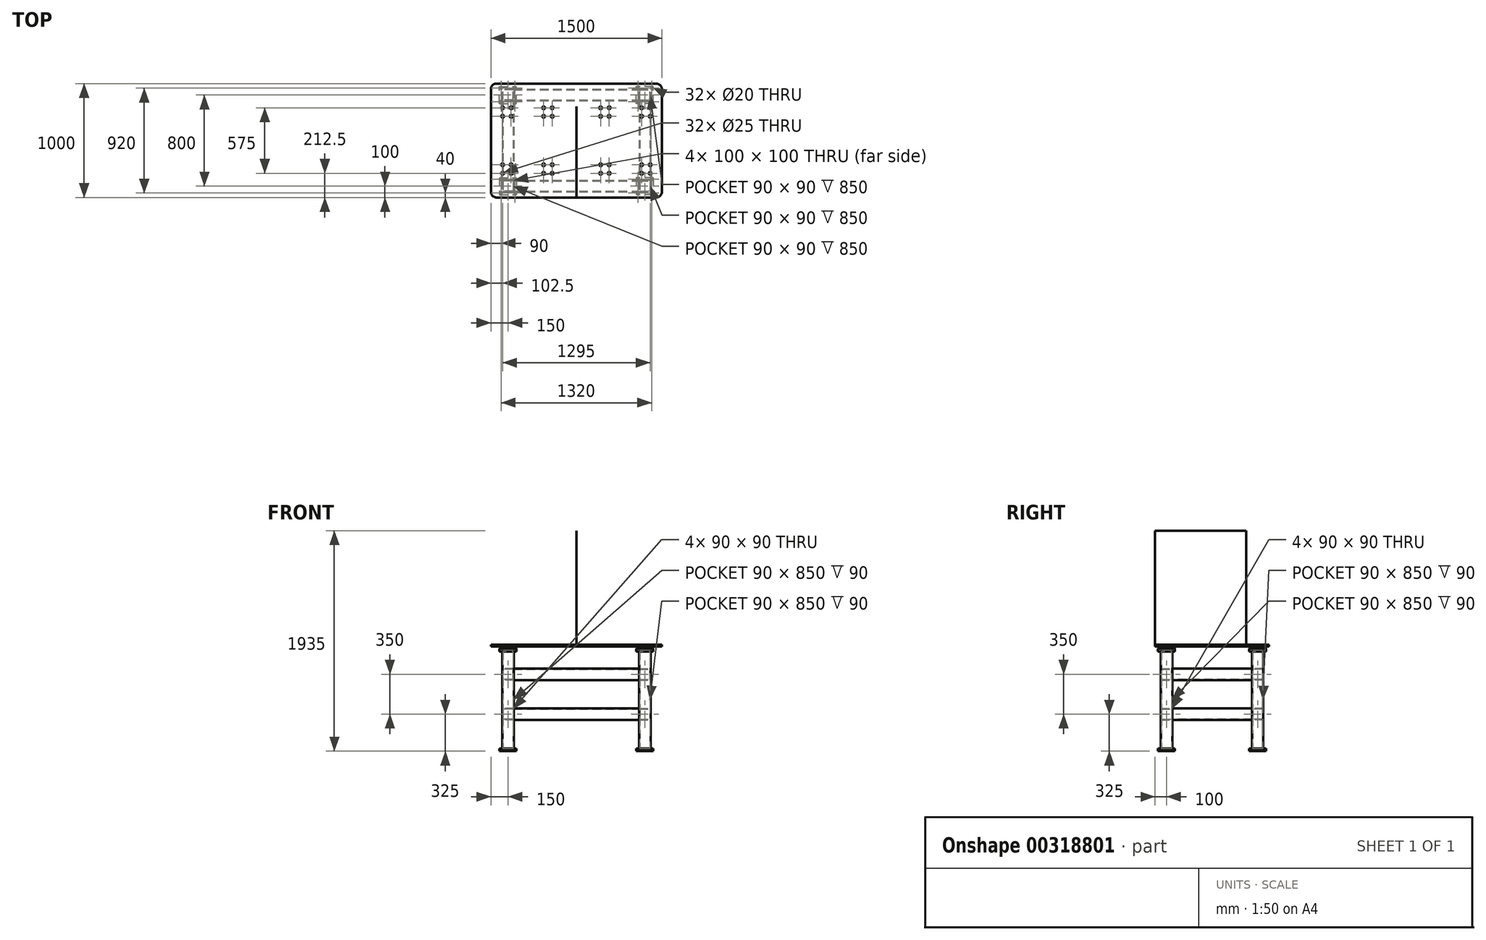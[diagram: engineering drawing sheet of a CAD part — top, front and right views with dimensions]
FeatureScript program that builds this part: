
annotation { "Feature Type Name" : "Feature", "Feature Type Description" : "" }
export const myFeature = defineFeature(function(context is Context, id is Id, definition is map)
    precondition{}
    {
        {
            var Q0;
            Q0=qCreatedBy(makeId("Top.planeOp"),FACE);
            var sketch = newSketch(context, id + "F0", { "sketchPlane" : qUnion([Q0])});
            skLineSegment(sketch, "E0.rect.bottom", {"start": v(-600, -400) * mm, "end": v(600, -400) * mm, "construction": true});
            skLineSegment(sketch, "E0.rect.top", {"start": v(-600, 400) * mm, "end": v(600, 400) * mm, "construction": true});
            skLineSegment(sketch, "E0.rect.left", {"start": v(-600, -400) * mm, "end": v(-600, 400) * mm, "construction": true});
            skLineSegment(sketch, "E0.rect.right", {"start": v(600, -400) * mm, "end": v(600, 400) * mm, "construction": true});
            skPoint(sketch, "E0.rect.middle", {"position": v(0, 0) * mm});
            skLineSegment(sketch, "E1.rect.bottom", {"start": v(-675, 325) * mm, "end": v(-525, 325) * mm});
            skLineSegment(sketch, "E1.rect.top", {"start": v(-675, 475) * mm, "end": v(-525, 475) * mm});
            skLineSegment(sketch, "E1.rect.left", {"start": v(-675, 325) * mm, "end": v(-675, 475) * mm});
            skLineSegment(sketch, "E1.rect.right", {"start": v(-525, 325) * mm, "end": v(-525, 475) * mm});
            skPoint(sketch, "E1.rect.middle", {"position": v(-600, 400) * mm});
            skLineSegment(sketch, "E2.rect.bottom", {"start": v(-660, 340) * mm, "end": v(-540, 340) * mm, "construction": true});
            skLineSegment(sketch, "E2.rect.top", {"start": v(-660, 460) * mm, "end": v(-540, 460) * mm, "construction": true});
            skLineSegment(sketch, "E2.rect.left", {"start": v(-660, 340) * mm, "end": v(-660, 460) * mm, "construction": true});
            skLineSegment(sketch, "E2.rect.right", {"start": v(-540, 340) * mm, "end": v(-540, 460) * mm, "construction": true});
            skCircle(sketch, "E3", {"center": v(-660, 460) * mm, "radius": 10 * mm});
            skCircle(sketch, "E4", {"center": v(-540, 460) * mm, "radius": 10 * mm});
            skCircle(sketch, "E5", {"center": v(-660, 340) * mm, "radius": 10 * mm});
            skCircle(sketch, "E6", {"center": v(-540, 340) * mm, "radius": 10 * mm});
            skCircle(sketch, "E7.MirrorC", {"center": v(540, 340) * mm, "radius": 10 * mm});
            skCircle(sketch, "E8.MirrorC", {"center": v(660, 460) * mm, "radius": 10 * mm});
            skCircle(sketch, "E9.MirrorC", {"center": v(660, 340) * mm, "radius": 10 * mm});
            skCircle(sketch, "E10.MirrorC", {"center": v(540, 460) * mm, "radius": 10 * mm});
            skPoint(sketch, "E11.MirrorP", {"position": v(600, 400) * mm});
            skLineSegment(sketch, "E12.MirrorCS", {"start": v(540, 340) * mm, "end": v(540, 460) * mm, "construction": true});
            skLineSegment(sketch, "E13.MirrorCS", {"start": v(660, 340) * mm, "end": v(660, 460) * mm, "construction": true});
            skLineSegment(sketch, "E14.MirrorCS", {"start": v(660, 460) * mm, "end": v(540, 460) * mm, "construction": true});
            skLineSegment(sketch, "E15.MirrorCS", {"start": v(675, 325) * mm, "end": v(525, 325) * mm});
            skLineSegment(sketch, "E16.MirrorCS", {"start": v(675, 475) * mm, "end": v(525, 475) * mm});
            skLineSegment(sketch, "E17.MirrorCS", {"start": v(675, 325) * mm, "end": v(675, 475) * mm});
            skLineSegment(sketch, "E18.MirrorCS", {"start": v(525, 325) * mm, "end": v(525, 475) * mm});
            skLineSegment(sketch, "E19.MirrorCS", {"start": v(660, 340) * mm, "end": v(540, 340) * mm, "construction": true});
            skCircle(sketch, "E20.MirrorC", {"center": v(540, -340) * mm, "radius": 10 * mm});
            skCircle(sketch, "E21.MirrorC", {"center": v(660, -340) * mm, "radius": 10 * mm});
            skCircle(sketch, "E22.MirrorC", {"center": v(-660, -460) * mm, "radius": 10 * mm});
            skCircle(sketch, "E23.MirrorC", {"center": v(-540, -340) * mm, "radius": 10 * mm});
            skCircle(sketch, "E24.MirrorC", {"center": v(-660, -340) * mm, "radius": 10 * mm});
            skCircle(sketch, "E25.MirrorC", {"center": v(-540, -460) * mm, "radius": 10 * mm});
            skCircle(sketch, "E26.MirrorC", {"center": v(660, -460) * mm, "radius": 10 * mm});
            skCircle(sketch, "E27.MirrorC", {"center": v(540, -460) * mm, "radius": 10 * mm});
            skPoint(sketch, "E28.MirrorP", {"position": v(600, -400) * mm});
            skPoint(sketch, "E29.MirrorP", {"position": v(-600, -400) * mm});
            skLineSegment(sketch, "E30.MirrorCS", {"start": v(540, -340) * mm, "end": v(540, -460) * mm, "construction": true});
            skLineSegment(sketch, "E31.MirrorCS", {"start": v(660, -460) * mm, "end": v(540, -460) * mm, "construction": true});
            skLineSegment(sketch, "E32.MirrorCS", {"start": v(675, -325) * mm, "end": v(525, -325) * mm});
            skLineSegment(sketch, "E33.MirrorCS", {"start": v(675, -325) * mm, "end": v(675, -475) * mm});
            skLineSegment(sketch, "E34.MirrorCS", {"start": v(660, -340) * mm, "end": v(540, -340) * mm, "construction": true});
            skLineSegment(sketch, "E35.MirrorCS", {"start": v(-540, -340) * mm, "end": v(-540, -460) * mm, "construction": true});
            skLineSegment(sketch, "E36.MirrorCS", {"start": v(-660, -340) * mm, "end": v(-660, -460) * mm, "construction": true});
            skLineSegment(sketch, "E37.MirrorCS", {"start": v(-660, -460) * mm, "end": v(-540, -460) * mm, "construction": true});
            skLineSegment(sketch, "E38.MirrorCS", {"start": v(-660, -340) * mm, "end": v(-540, -340) * mm, "construction": true});
            skLineSegment(sketch, "E39.MirrorCS", {"start": v(-525, -325) * mm, "end": v(-525, -475) * mm});
            skLineSegment(sketch, "E40.MirrorCS", {"start": v(-675, -325) * mm, "end": v(-675, -475) * mm});
            skLineSegment(sketch, "E41.MirrorCS", {"start": v(-675, -475) * mm, "end": v(-525, -475) * mm});
            skLineSegment(sketch, "E42.MirrorCS", {"start": v(-600, -400) * mm, "end": v(600, -400) * mm});
            skLineSegment(sketch, "E43.MirrorCS", {"start": v(525, -325) * mm, "end": v(525, -475) * mm});
            skLineSegment(sketch, "E44.MirrorCS", {"start": v(-675, -325) * mm, "end": v(-525, -325) * mm});
            skLineSegment(sketch, "E45.MirrorCS", {"start": v(660, -340) * mm, "end": v(660, -460) * mm, "construction": true});
            skLineSegment(sketch, "E46.MirrorCS", {"start": v(675, -475) * mm, "end": v(525, -475) * mm});
            skSolve(sketch);
        }
        {
            var Q0;
            Q0=qSketchRegion(id+"F0",true);
            extrude(context, id + "F1", {"entities" : qUnion([Q0]), "depth" : 25 * mm});
        }
        {
            var Q0;
            Q0=makeQuery(id+"F1.opExtrude","CAP_FACE",FACE,{"disambiguationData":[OSD([sQuery(id+"F0.wireOp",EDGE,"E1.rect.bottom"),sQuery(id+"F0.wireOp",EDGE,"E1.rect.top"),sQuery(id+"F0.wireOp",EDGE,"E1.rect.left"),sQuery(id+"F0.wireOp",EDGE,"E1.rect.right"),sQuery(id+"F0.wireOp",EDGE,"E3"),sQuery(id+"F0.wireOp",EDGE,"E4"),sQuery(id+"F0.wireOp",EDGE,"E5"),sQuery(id+"F0.wireOp",EDGE,"E6")])],"isStart":false});
            var sketch = newSketch(context, id + "F2", { "sketchPlane" : qUnion([Q0])});
            skLineSegment(sketch, "E47.rect.bottom", {"start": v(-550, 350) * mm, "end": v(-650, 350) * mm});
            skLineSegment(sketch, "E47.rect.top", {"start": v(-550, 450) * mm, "end": v(-650, 450) * mm});
            skLineSegment(sketch, "E47.rect.left", {"start": v(-550, 350) * mm, "end": v(-550, 450) * mm});
            skLineSegment(sketch, "E47.rect.right", {"start": v(-650, 350) * mm, "end": v(-650, 450) * mm});
            skPoint(sketch, "E47.rect.middle", {"position": v(-600, 400) * mm});
            skPoint(sketch, "E47.rect.middle.positionSnap0", {"position": v(-675, 400) * mm});
            skPoint(sketch, "E47.rect.centerSnap0", {"position": v(-675, 400) * mm});
            skLineSegment(sketch, "E48.rect.bottom", {"start": v(-555, 355) * mm, "end": v(-645, 355) * mm});
            skLineSegment(sketch, "E48.rect.top", {"start": v(-555, 445) * mm, "end": v(-645, 445) * mm});
            skLineSegment(sketch, "E48.rect.left", {"start": v(-555, 355) * mm, "end": v(-555, 445) * mm});
            skLineSegment(sketch, "E48.rect.right", {"start": v(-645, 355) * mm, "end": v(-645, 445) * mm});
            skPoint(sketch, "E49.MirrorP", {"position": v(600, 400) * mm});
            skPoint(sketch, "E50.MirrorP", {"position": v(675, 400) * mm});
            skLineSegment(sketch, "E51.MirrorCS", {"start": v(645, 355) * mm, "end": v(645, 445) * mm});
            skLineSegment(sketch, "E52.MirrorCS", {"start": v(555, 355) * mm, "end": v(555, 445) * mm});
            skLineSegment(sketch, "E53.MirrorCS", {"start": v(555, 445) * mm, "end": v(645, 445) * mm});
            skLineSegment(sketch, "E54.MirrorCS", {"start": v(555, 355) * mm, "end": v(645, 355) * mm});
            skLineSegment(sketch, "E55.MirrorCS", {"start": v(650, 350) * mm, "end": v(650, 450) * mm});
            skLineSegment(sketch, "E56.MirrorCS", {"start": v(550, 350) * mm, "end": v(650, 350) * mm});
            skLineSegment(sketch, "E57.MirrorCS", {"start": v(550, 350) * mm, "end": v(550, 450) * mm});
            skLineSegment(sketch, "E58.MirrorCS", {"start": v(550, 450) * mm, "end": v(650, 450) * mm});
            skLineSegment(sketch, "E59.MirrorCS", {"start": v(650, -350) * mm, "end": v(650, -450) * mm});
            skPoint(sketch, "E60.MirrorP", {"position": v(-675, -400) * mm});
            skPoint(sketch, "E61.MirrorP", {"position": v(600, -400) * mm});
            skPoint(sketch, "E62.MirrorP", {"position": v(-600, -400) * mm});
            skPoint(sketch, "E63.MirrorP", {"position": v(675, -400) * mm});
            skLineSegment(sketch, "E64.MirrorCS", {"start": v(-555, -355) * mm, "end": v(-555, -445) * mm});
            skLineSegment(sketch, "E65.MirrorCS", {"start": v(-555, -445) * mm, "end": v(-645, -445) * mm});
            skLineSegment(sketch, "E66.MirrorCS", {"start": v(-555, -355) * mm, "end": v(-645, -355) * mm});
            skLineSegment(sketch, "E67.MirrorCS", {"start": v(-650, -350) * mm, "end": v(-650, -450) * mm});
            skLineSegment(sketch, "E68.MirrorCS", {"start": v(-550, -350) * mm, "end": v(-550, -450) * mm});
            skLineSegment(sketch, "E69.MirrorCS", {"start": v(-550, -450) * mm, "end": v(-650, -450) * mm});
            skLineSegment(sketch, "E70.MirrorCS", {"start": v(-550, -350) * mm, "end": v(-650, -350) * mm});
            skLineSegment(sketch, "E71.MirrorCS", {"start": v(550, -450) * mm, "end": v(650, -450) * mm});
            skLineSegment(sketch, "E72.MirrorCS", {"start": v(550, -350) * mm, "end": v(550, -450) * mm});
            skLineSegment(sketch, "E73.MirrorCS", {"start": v(550, -350) * mm, "end": v(650, -350) * mm});
            skLineSegment(sketch, "E74.MirrorCS", {"start": v(-645, -355) * mm, "end": v(-645, -445) * mm});
            skLineSegment(sketch, "E75.MirrorCS", {"start": v(645, -355) * mm, "end": v(645, -445) * mm});
            skLineSegment(sketch, "E76.MirrorCS", {"start": v(555, -355) * mm, "end": v(555, -445) * mm});
            skLineSegment(sketch, "E77.MirrorCS", {"start": v(555, -355) * mm, "end": v(645, -355) * mm});
            skLineSegment(sketch, "E78.MirrorCS", {"start": v(555, -445) * mm, "end": v(645, -445) * mm});
            skSolve(sketch);
        }
        {
            var Q0;
            Q0=qSketchRegion(id+"F2",true);
            extrude(context, id + "F3", {"entities" : qUnion([Q0]), "operationType" : NewBodyOperationType.ADD, "depth" : 850 * mm});
        }
        {
            var Q0;
            Q0=makeQuery(id+"F3.opExtrude","CAP_FACE",FACE,{"disambiguationData":[OSD([sQuery(id+"F2.wireOp",EDGE,"E47.rect.bottom"),sQuery(id+"F2.wireOp",EDGE,"E47.rect.top"),sQuery(id+"F2.wireOp",EDGE,"E47.rect.left"),sQuery(id+"F2.wireOp",EDGE,"E47.rect.right"),sQuery(id+"F2.wireOp",EDGE,"E48.rect.bottom"),sQuery(id+"F2.wireOp",EDGE,"E48.rect.top"),sQuery(id+"F2.wireOp",EDGE,"E48.rect.left"),sQuery(id+"F2.wireOp",EDGE,"E48.rect.right")])],"isStart":false});
            var sketch = newSketch(context, id + "F4", { "sketchPlane" : qUnion([Q0])});
            skLineSegment(sketch, "E79.rect.bottom", {"start": v(-600, -400) * mm, "end": v(600, -400) * mm, "construction": true});
            skLineSegment(sketch, "E79.rect.top", {"start": v(-600, 400) * mm, "end": v(600, 400) * mm, "construction": true});
            skLineSegment(sketch, "E79.rect.left", {"start": v(-600, -400) * mm, "end": v(-600, 400) * mm, "construction": true});
            skLineSegment(sketch, "E79.rect.right", {"start": v(600, -400) * mm, "end": v(600, 400) * mm, "construction": true});
            skLineSegment(sketch, "E80.rect.bottom", {"start": v(-675, 325) * mm, "end": v(-525, 325) * mm});
            skLineSegment(sketch, "E80.rect.top", {"start": v(-675, 475) * mm, "end": v(-525, 475) * mm});
            skLineSegment(sketch, "E80.rect.left", {"start": v(-675, 325) * mm, "end": v(-675, 475) * mm});
            skLineSegment(sketch, "E80.rect.right", {"start": v(-525, 325) * mm, "end": v(-525, 475) * mm});
            skPoint(sketch, "E80.rect.middle", {"position": v(-600, 400) * mm});
            skLineSegment(sketch, "E81.rect.bottom", {"start": v(-660, 340) * mm, "end": v(-540, 340) * mm, "construction": true});
            skLineSegment(sketch, "E81.rect.top", {"start": v(-660, 460) * mm, "end": v(-540, 460) * mm, "construction": true});
            skLineSegment(sketch, "E81.rect.left", {"start": v(-660, 340) * mm, "end": v(-660, 460) * mm, "construction": true});
            skLineSegment(sketch, "E81.rect.right", {"start": v(-540, 340) * mm, "end": v(-540, 460) * mm, "construction": true});
            skCircle(sketch, "E82", {"center": v(-660, 460) * mm, "radius": 10 * mm});
            skCircle(sketch, "E83", {"center": v(-540, 460) * mm, "radius": 10 * mm});
            skCircle(sketch, "E84", {"center": v(-660, 340) * mm, "radius": 10 * mm});
            skCircle(sketch, "E85", {"center": v(-540, 340) * mm, "radius": 10 * mm});
            skPoint(sketch, "E86.MirrorP", {"position": v(600, 400) * mm});
            skPoint(sketch, "E87.MirrorP", {"position": v(-1214.7, -400) * mm});
            skLineSegment(sketch, "E88.MirrorCS", {"start": v(-1214.7, -400) * mm, "end": v(-14.7, -400) * mm});
            skCircle(sketch, "E89.MirrorC", {"center": v(540, 340) * mm, "radius": 10 * mm});
            skCircle(sketch, "E90.MirrorC", {"center": v(660, 460) * mm, "radius": 10 * mm});
            skCircle(sketch, "E91.MirrorC", {"center": v(660, 340) * mm, "radius": 10 * mm});
            skCircle(sketch, "E92.MirrorC", {"center": v(540, 460) * mm, "radius": 10 * mm});
            skLineSegment(sketch, "E93.MirrorCS", {"start": v(660, 340) * mm, "end": v(540, 340) * mm, "construction": true});
            skLineSegment(sketch, "E94.MirrorCS", {"start": v(525, 325) * mm, "end": v(525, 475) * mm});
            skLineSegment(sketch, "E95.MirrorCS", {"start": v(675, 325) * mm, "end": v(675, 475) * mm});
            skLineSegment(sketch, "E96.MirrorCS", {"start": v(540, 340) * mm, "end": v(540, 460) * mm, "construction": true});
            skLineSegment(sketch, "E97.MirrorCS", {"start": v(675, 475) * mm, "end": v(525, 475) * mm});
            skLineSegment(sketch, "E98.MirrorCS", {"start": v(660, 340) * mm, "end": v(660, 460) * mm, "construction": true});
            skLineSegment(sketch, "E99.MirrorCS", {"start": v(660, 460) * mm, "end": v(540, 460) * mm, "construction": true});
            skLineSegment(sketch, "E100.MirrorCS", {"start": v(675, 325) * mm, "end": v(525, 325) * mm});
            skCircle(sketch, "E101.MirrorC", {"center": v(-660, -460) * mm, "radius": 10 * mm});
            skPoint(sketch, "E102.MirrorP", {"position": v(600, -400) * mm});
            skCircle(sketch, "E103.MirrorC", {"center": v(660, -460) * mm, "radius": 10 * mm});
            skCircle(sketch, "E104.MirrorC", {"center": v(-540, -340) * mm, "radius": 10 * mm});
            skCircle(sketch, "E105.MirrorC", {"center": v(-660, -340) * mm, "radius": 10 * mm});
            skCircle(sketch, "E106.MirrorC", {"center": v(660, -340) * mm, "radius": 10 * mm});
            skCircle(sketch, "E107.MirrorC", {"center": v(540, -460) * mm, "radius": 10 * mm});
            skCircle(sketch, "E108.MirrorC", {"center": v(-540, -460) * mm, "radius": 10 * mm});
            skCircle(sketch, "E109.MirrorC", {"center": v(540, -340) * mm, "radius": 10 * mm});
            skPoint(sketch, "E110.MirrorP", {"position": v(-600, -400) * mm});
            skLineSegment(sketch, "E111.MirrorCS", {"start": v(660, -340) * mm, "end": v(540, -340) * mm, "construction": true});
            skLineSegment(sketch, "E112.MirrorCS", {"start": v(-540, -340) * mm, "end": v(-540, -460) * mm, "construction": true});
            skLineSegment(sketch, "E113.MirrorCS", {"start": v(660, -460) * mm, "end": v(540, -460) * mm, "construction": true});
            skLineSegment(sketch, "E114.MirrorCS", {"start": v(675, -325) * mm, "end": v(525, -325) * mm});
            skLineSegment(sketch, "E115.MirrorCS", {"start": v(-660, -340) * mm, "end": v(-660, -460) * mm, "construction": true});
            skLineSegment(sketch, "E116.MirrorCS", {"start": v(-660, -460) * mm, "end": v(-540, -460) * mm, "construction": true});
            skLineSegment(sketch, "E117.MirrorCS", {"start": v(540, -340) * mm, "end": v(540, -460) * mm, "construction": true});
            skLineSegment(sketch, "E118.MirrorCS", {"start": v(-660, -340) * mm, "end": v(-540, -340) * mm, "construction": true});
            skLineSegment(sketch, "E119.MirrorCS", {"start": v(-525, -325) * mm, "end": v(-525, -475) * mm});
            skLineSegment(sketch, "E120.MirrorCS", {"start": v(675, -475) * mm, "end": v(525, -475) * mm});
            skLineSegment(sketch, "E121.MirrorCS", {"start": v(525, -325) * mm, "end": v(525, -475) * mm});
            skLineSegment(sketch, "E122.MirrorCS", {"start": v(-675, -475) * mm, "end": v(-525, -475) * mm});
            skLineSegment(sketch, "E123.MirrorCS", {"start": v(660, -340) * mm, "end": v(660, -460) * mm, "construction": true});
            skLineSegment(sketch, "E124.MirrorCS", {"start": v(-675, -325) * mm, "end": v(-675, -475) * mm});
            skLineSegment(sketch, "E125.MirrorCS", {"start": v(-600, -400) * mm, "end": v(600, -400) * mm});
            skLineSegment(sketch, "E126.MirrorCS", {"start": v(675, -325) * mm, "end": v(675, -475) * mm});
            skLineSegment(sketch, "E127.MirrorCS", {"start": v(-675, -325) * mm, "end": v(-525, -325) * mm});
            skSolve(sketch);
        }
        {
            var Q0;
            Q0=qSketchRegion(id+"F4",true);
            extrude(context, id + "F5", {"entities" : qUnion([Q0]), "operationType" : NewBodyOperationType.ADD, "depth" : 25 * mm});
        }
        {
            var Q0;
            Q0=makeQuery(id+"F3.opExtrude","SWEPT_FACE",FACE,{"disambiguationData":[OSD([sQuery(id+"F2.wireOp",EDGE,"E72.MirrorCS")])]});
            var sketch = newSketch(context, id + "F6", { "sketchPlane" : qUnion([Q0])});
            skLineSegment(sketch, "E128", {"start": v(350, 875) * mm, "end": v(350, 725) * mm, "construction": true});
            skLineSegment(sketch, "E129", {"start": v(350, 25) * mm, "end": v(350, 275) * mm, "construction": true});
            skLineSegment(sketch, "E130.bottom", {"start": v(350, 725) * mm, "end": v(450, 725) * mm});
            skLineSegment(sketch, "E130.top", {"start": v(350, 625) * mm, "end": v(450, 625) * mm});
            skLineSegment(sketch, "E130.left", {"start": v(350, 725) * mm, "end": v(350, 625) * mm});
            skLineSegment(sketch, "E130.right", {"start": v(450, 725) * mm, "end": v(450, 625) * mm});
            skLineSegment(sketch, "E131.bottom", {"start": v(355, 720) * mm, "end": v(445, 720) * mm});
            skLineSegment(sketch, "E131.top", {"start": v(355, 630) * mm, "end": v(445, 630) * mm});
            skLineSegment(sketch, "E131.left", {"start": v(355, 720) * mm, "end": v(355, 630) * mm});
            skLineSegment(sketch, "E131.right", {"start": v(445, 720) * mm, "end": v(445, 630) * mm});
            skLineSegment(sketch, "E132.bottom", {"start": v(350, 275) * mm, "end": v(450, 275) * mm});
            skLineSegment(sketch, "E132.top", {"start": v(350, 375) * mm, "end": v(450, 375) * mm});
            skLineSegment(sketch, "E132.left", {"start": v(350, 275) * mm, "end": v(350, 375) * mm});
            skLineSegment(sketch, "E132.right", {"start": v(450, 275) * mm, "end": v(450, 375) * mm});
            skLineSegment(sketch, "E133.bottom", {"start": v(355, 280) * mm, "end": v(445, 280) * mm});
            skLineSegment(sketch, "E133.top", {"start": v(355, 370) * mm, "end": v(445, 370) * mm});
            skLineSegment(sketch, "E133.left", {"start": v(355, 280) * mm, "end": v(355, 370) * mm});
            skLineSegment(sketch, "E133.right", {"start": v(445, 280) * mm, "end": v(445, 370) * mm});
            skLineSegment(sketch, "E134.MirrorCS", {"start": v(-350, 725) * mm, "end": v(-450, 725) * mm});
            skLineSegment(sketch, "E135.MirrorCS", {"start": v(-355, 720) * mm, "end": v(-445, 720) * mm});
            skLineSegment(sketch, "E136.MirrorCS", {"start": v(-450, 725) * mm, "end": v(-450, 625) * mm});
            skLineSegment(sketch, "E137.MirrorCS", {"start": v(-445, 720) * mm, "end": v(-445, 630) * mm});
            skLineSegment(sketch, "E138.MirrorCS", {"start": v(-355, 720) * mm, "end": v(-355, 630) * mm});
            skLineSegment(sketch, "E139.MirrorCS", {"start": v(-350, 725) * mm, "end": v(-350, 625) * mm});
            skLineSegment(sketch, "E140.MirrorCS", {"start": v(-355, 630) * mm, "end": v(-445, 630) * mm});
            skLineSegment(sketch, "E141.MirrorCS", {"start": v(-350, 625) * mm, "end": v(-450, 625) * mm});
            skLineSegment(sketch, "E142.MirrorCS", {"start": v(-350, 375) * mm, "end": v(-450, 375) * mm});
            skLineSegment(sketch, "E143.MirrorCS", {"start": v(-355, 370) * mm, "end": v(-445, 370) * mm});
            skLineSegment(sketch, "E144.MirrorCS", {"start": v(-450, 275) * mm, "end": v(-450, 375) * mm});
            skLineSegment(sketch, "E145.MirrorCS", {"start": v(-445, 280) * mm, "end": v(-445, 370) * mm});
            skLineSegment(sketch, "E146.MirrorCS", {"start": v(-355, 280) * mm, "end": v(-355, 370) * mm});
            skLineSegment(sketch, "E147.MirrorCS", {"start": v(-350, 275) * mm, "end": v(-350, 375) * mm});
            skLineSegment(sketch, "E148.MirrorCS", {"start": v(-355, 280) * mm, "end": v(-445, 280) * mm});
            skLineSegment(sketch, "E149.MirrorCS", {"start": v(-350, 275) * mm, "end": v(-450, 275) * mm});
            skSolve(sketch);
        }
        {
            var Q0;
            Q0=qSketchRegion(id+"F6",true);
            var Q1;
            Q1=makeQuery(id+"F3.opExtrude","SWEPT_FACE",FACE,{"disambiguationData":[OSD([sQuery(id+"F2.wireOp",EDGE,"E68.MirrorCS")])]});
            extrude(context, id + "F7", {"entities" : qUnion([Q0]), "endBound" : BoundingType.UP_TO_SURFACE, "endBoundEntityFace" : qUnion([Q1]), "depth" : 25 * mm});
        }
        {
            var Q0;
            Q0=makeQuery(id+"F3.opExtrude","SWEPT_FACE",FACE,{"disambiguationData":[OSD([sQuery(id+"F2.wireOp",EDGE,"E73.MirrorCS")])]});
            var sketch = newSketch(context, id + "F8", { "sketchPlane" : qUnion([Q0])});
            skLineSegment(sketch, "E150", {"start": v(-650, 875) * mm, "end": v(-650, 725) * mm, "construction": true});
            skLineSegment(sketch, "E151", {"start": v(-650, 25) * mm, "end": v(-650, 275) * mm, "construction": true});
            skLineSegment(sketch, "E152.bottom", {"start": v(-650, 725) * mm, "end": v(-550, 725) * mm});
            skLineSegment(sketch, "E152.top", {"start": v(-650, 625) * mm, "end": v(-550, 625) * mm});
            skLineSegment(sketch, "E152.left", {"start": v(-650, 725) * mm, "end": v(-650, 625) * mm});
            skLineSegment(sketch, "E152.right", {"start": v(-550, 725) * mm, "end": v(-550, 625) * mm});
            skLineSegment(sketch, "E153.bottom", {"start": v(-645, 720) * mm, "end": v(-555, 720) * mm});
            skLineSegment(sketch, "E153.top", {"start": v(-645, 630) * mm, "end": v(-555, 630) * mm});
            skLineSegment(sketch, "E153.left", {"start": v(-645, 720) * mm, "end": v(-645, 630) * mm});
            skLineSegment(sketch, "E153.right", {"start": v(-555, 720) * mm, "end": v(-555, 630) * mm});
            skLineSegment(sketch, "E154.bottom", {"start": v(-650, 275) * mm, "end": v(-550, 275) * mm});
            skLineSegment(sketch, "E154.top", {"start": v(-650, 375) * mm, "end": v(-550, 375) * mm});
            skLineSegment(sketch, "E154.left", {"start": v(-650, 275) * mm, "end": v(-650, 375) * mm});
            skLineSegment(sketch, "E154.right", {"start": v(-550, 275) * mm, "end": v(-550, 375) * mm});
            skLineSegment(sketch, "E155.bottom", {"start": v(-645, 280) * mm, "end": v(-555, 280) * mm});
            skLineSegment(sketch, "E155.top", {"start": v(-645, 370) * mm, "end": v(-555, 370) * mm});
            skLineSegment(sketch, "E155.left", {"start": v(-645, 280) * mm, "end": v(-645, 370) * mm});
            skLineSegment(sketch, "E155.right", {"start": v(-555, 280) * mm, "end": v(-555, 370) * mm});
            skLineSegment(sketch, "E156.MirrorCS", {"start": v(650, 875) * mm, "end": v(650, 725) * mm});
            skLineSegment(sketch, "E157.MirrorCS", {"start": v(650, 725) * mm, "end": v(550, 725) * mm});
            skLineSegment(sketch, "E158.MirrorCS", {"start": v(645, 720) * mm, "end": v(555, 720) * mm});
            skLineSegment(sketch, "E159.MirrorCS", {"start": v(550, 725) * mm, "end": v(550, 625) * mm});
            skLineSegment(sketch, "E160.MirrorCS", {"start": v(555, 720) * mm, "end": v(555, 630) * mm});
            skLineSegment(sketch, "E161.MirrorCS", {"start": v(645, 720) * mm, "end": v(645, 630) * mm});
            skLineSegment(sketch, "E162.MirrorCS", {"start": v(650, 725) * mm, "end": v(650, 625) * mm});
            skLineSegment(sketch, "E163.MirrorCS", {"start": v(645, 630) * mm, "end": v(555, 630) * mm});
            skLineSegment(sketch, "E164.MirrorCS", {"start": v(650, 625) * mm, "end": v(550, 625) * mm});
            skLineSegment(sketch, "E165.MirrorCS", {"start": v(650, 375) * mm, "end": v(550, 375) * mm});
            skLineSegment(sketch, "E166.MirrorCS", {"start": v(645, 370) * mm, "end": v(555, 370) * mm});
            skLineSegment(sketch, "E167.MirrorCS", {"start": v(550, 275) * mm, "end": v(550, 375) * mm});
            skLineSegment(sketch, "E168.MirrorCS", {"start": v(555, 280) * mm, "end": v(555, 370) * mm});
            skLineSegment(sketch, "E169.MirrorCS", {"start": v(645, 280) * mm, "end": v(645, 370) * mm});
            skLineSegment(sketch, "E170.MirrorCS", {"start": v(650, 275) * mm, "end": v(650, 375) * mm});
            skLineSegment(sketch, "E171.MirrorCS", {"start": v(645, 280) * mm, "end": v(555, 280) * mm});
            skLineSegment(sketch, "E172.MirrorCS", {"start": v(650, 275) * mm, "end": v(550, 275) * mm});
            skSolve(sketch);
        }
        {
            var Q0;
            Q0=qSketchRegion(id+"F8",true);
            var Q1;
            Q1=makeQuery(id+"F3.opExtrude","SWEPT_FACE",FACE,{"disambiguationData":[OSD([sQuery(id+"F2.wireOp",EDGE,"E47.rect.bottom")])]});
            extrude(context, id + "F9", {"entities" : qUnion([Q0]), "endBound" : BoundingType.UP_TO_SURFACE, "endBoundEntityFace" : qUnion([Q1]), "depth" : 25 * mm});
        }
        {
            var Q0;
            Q0=makeQuery(id+"F5.opExtrude","CAP_FACE",FACE,{"disambiguationData":[OSD([sQuery(id+"F4.wireOp",EDGE,"E80.rect.bottom"),sQuery(id+"F4.wireOp",EDGE,"E80.rect.top"),sQuery(id+"F4.wireOp",EDGE,"E80.rect.left"),sQuery(id+"F4.wireOp",EDGE,"E80.rect.right"),sQuery(id+"F4.wireOp",EDGE,"E82"),sQuery(id+"F4.wireOp",EDGE,"E83"),sQuery(id+"F4.wireOp",EDGE,"E84"),sQuery(id+"F4.wireOp",EDGE,"E85")])],"isStart":false});
            var sketch = newSketch(context, id + "F10", { "sketchPlane" : qUnion([Q0])});
            skLineSegment(sketch, "E173.rect.bottom", {"start": v(-750, 500) * mm, "end": v(750, 500) * mm});
            skLineSegment(sketch, "E173.rect.top", {"start": v(-750, -500) * mm, "end": v(750, -500) * mm});
            skLineSegment(sketch, "E173.rect.left", {"start": v(-750, 500) * mm, "end": v(-750, -500) * mm});
            skLineSegment(sketch, "E173.rect.right", {"start": v(750, 500) * mm, "end": v(750, -500) * mm});
            skPoint(sketch, "E173.rect.middle", {"position": v(0, 0) * mm});
            skSolve(sketch);
        }
        {
            var Q0;
            Q0=qSketchRegion(id+"F10",true);
            extrude(context, id + "F11", {"entities" : qUnion([Q0]), "depth" : 35 * mm});
        }
        {
            var Q0;
            Q0=makeQuery(id+"F11.opExtrude","CAP_FACE",FACE,{"disambiguationData":[OSD([sQuery(id+"F10.wireOp",EDGE,"E173.rect.bottom"),sQuery(id+"F10.wireOp",EDGE,"E173.rect.top"),sQuery(id+"F10.wireOp",EDGE,"E173.rect.left"),sQuery(id+"F10.wireOp",EDGE,"E173.rect.right")])],"isStart":true});
            var sketch = newSketch(context, id + "F12", { "sketchPlane" : qUnion([Q0])});
            skCircle(sketch, "E174.0", {"center": v(-660, 460) * mm, "radius": 10 * mm});
            skCircle(sketch, "E174.1", {"center": v(-540, 460) * mm, "radius": 10 * mm});
            skCircle(sketch, "E174.2", {"center": v(-660, 340) * mm, "radius": 10 * mm});
            skCircle(sketch, "E174.3", {"center": v(-540, 340) * mm, "radius": 10 * mm});
            skCircle(sketch, "E175.0", {"center": v(-660, -460) * mm, "radius": 10 * mm});
            skCircle(sketch, "E175.1", {"center": v(-660, -340) * mm, "radius": 10 * mm});
            skCircle(sketch, "E175.2", {"center": v(-540, -340) * mm, "radius": 10 * mm});
            skCircle(sketch, "E175.3", {"center": v(-540, -460) * mm, "radius": 10 * mm});
            skCircle(sketch, "E175.4", {"center": v(540, -340) * mm, "radius": 10 * mm});
            skCircle(sketch, "E175.5", {"center": v(660, -340) * mm, "radius": 10 * mm});
            skCircle(sketch, "E175.6", {"center": v(540, -460) * mm, "radius": 10 * mm});
            skCircle(sketch, "E175.7", {"center": v(660, -460) * mm, "radius": 10 * mm});
            skCircle(sketch, "E175.8", {"center": v(540, 460) * mm, "radius": 10 * mm});
            skCircle(sketch, "E175.9", {"center": v(660, 460) * mm, "radius": 10 * mm});
            skCircle(sketch, "E175.10", {"center": v(540, 340) * mm, "radius": 10 * mm});
            skCircle(sketch, "E175.11", {"center": v(660, 340) * mm, "radius": 10 * mm});
            skSolve(sketch);
        }
        {
            var Q0;
            Q0=makeQuery(id+"F12.imprint","IMPRINT",FACE,{"disambiguationData":[TD([[makeQuery(id+"F12.imprint","IMPRINT",EDGE,{"derivedFrom":sQuery(id+"F12.wireOp",EDGE,"E175.0")}),-1.0]])]});
            var Q1;
            Q1=makeQuery(id+"F12.imprint","IMPRINT",FACE,{"disambiguationData":[TD([[makeQuery(id+"F12.imprint","IMPRINT",EDGE,{"derivedFrom":sQuery(id+"F12.wireOp",EDGE,"E175.1")}),-1.0]])]});
            var Q2;
            Q2=makeQuery(id+"F12.imprint","IMPRINT",FACE,{"disambiguationData":[TD([[makeQuery(id+"F12.imprint","IMPRINT",EDGE,{"derivedFrom":sQuery(id+"F12.wireOp",EDGE,"E175.2")}),-1.0]])]});
            var Q3;
            Q3=makeQuery(id+"F12.imprint","IMPRINT",FACE,{"disambiguationData":[TD([[makeQuery(id+"F12.imprint","IMPRINT",EDGE,{"derivedFrom":sQuery(id+"F12.wireOp",EDGE,"E175.3")}),-1.0]])]});
            var Q4;
            Q4=makeQuery(id+"F12.imprint","IMPRINT",FACE,{"disambiguationData":[TD([[makeQuery(id+"F12.imprint","IMPRINT",EDGE,{"derivedFrom":sQuery(id+"F12.wireOp",EDGE,"E174.2")}),1.0]])]});
            var Q5;
            Q5=makeQuery(id+"F12.imprint","IMPRINT",FACE,{"disambiguationData":[TD([[makeQuery(id+"F12.imprint","IMPRINT",EDGE,{"derivedFrom":sQuery(id+"F12.wireOp",EDGE,"E174.0")}),1.0]])]});
            var Q6;
            Q6=makeQuery(id+"F12.imprint","IMPRINT",FACE,{"disambiguationData":[TD([[makeQuery(id+"F12.imprint","IMPRINT",EDGE,{"derivedFrom":sQuery(id+"F12.wireOp",EDGE,"E174.1")}),1.0]])]});
            var Q7;
            Q7=makeQuery(id+"F12.imprint","IMPRINT",FACE,{"disambiguationData":[TD([[makeQuery(id+"F12.imprint","IMPRINT",EDGE,{"derivedFrom":sQuery(id+"F12.wireOp",EDGE,"E174.3")}),1.0]])]});
            var Q8;
            Q8=makeQuery(id+"F12.imprint","IMPRINT",FACE,{"disambiguationData":[TD([[makeQuery(id+"F12.imprint","IMPRINT",EDGE,{"derivedFrom":sQuery(id+"F12.wireOp",EDGE,"E175.8")}),-1.0]])]});
            var Q9;
            Q9=makeQuery(id+"F12.imprint","IMPRINT",FACE,{"disambiguationData":[TD([[makeQuery(id+"F12.imprint","IMPRINT",EDGE,{"derivedFrom":sQuery(id+"F12.wireOp",EDGE,"E175.9")}),-1.0]])]});
            var Q10;
            Q10=makeQuery(id+"F12.imprint","IMPRINT",FACE,{"disambiguationData":[TD([[makeQuery(id+"F12.imprint","IMPRINT",EDGE,{"derivedFrom":sQuery(id+"F12.wireOp",EDGE,"E175.11")}),-1.0]])]});
            var Q11;
            Q11=makeQuery(id+"F12.imprint","IMPRINT",FACE,{"disambiguationData":[TD([[makeQuery(id+"F12.imprint","IMPRINT",EDGE,{"derivedFrom":sQuery(id+"F12.wireOp",EDGE,"E175.10")}),-1.0]])]});
            var Q12;
            Q12=makeQuery(id+"F12.imprint","IMPRINT",FACE,{"disambiguationData":[TD([[makeQuery(id+"F12.imprint","IMPRINT",EDGE,{"derivedFrom":sQuery(id+"F12.wireOp",EDGE,"E175.5")}),1.0]])]});
            var Q13;
            Q13=makeQuery(id+"F12.imprint","IMPRINT",FACE,{"disambiguationData":[TD([[makeQuery(id+"F12.imprint","IMPRINT",EDGE,{"derivedFrom":sQuery(id+"F12.wireOp",EDGE,"E175.4")}),1.0]])]});
            var Q14;
            Q14=makeQuery(id+"F12.imprint","IMPRINT",FACE,{"disambiguationData":[TD([[makeQuery(id+"F12.imprint","IMPRINT",EDGE,{"derivedFrom":sQuery(id+"F12.wireOp",EDGE,"E175.7")}),1.0]])]});
            var Q15;
            Q15=makeQuery(id+"F12.imprint","IMPRINT",FACE,{"disambiguationData":[TD([[makeQuery(id+"F12.imprint","IMPRINT",EDGE,{"derivedFrom":sQuery(id+"F12.wireOp",EDGE,"E175.6")}),1.0]])]});
            extrude(context, id + "F13", {"entities" : qUnion([Q0, Q1, Q2, Q3, Q4, Q5, Q6, Q7, Q8, Q9, Q10, Q11, Q12, Q13, Q14, Q15]), "operationType" : NewBodyOperationType.REMOVE, "oppositeDirection" : true, "depth" : 20 * mm});
        }
        {
            var Q0;
            Q0=makeQuery(id+"F11.opExtrude","SWEPT_EDGE",EDGE,{"disambiguationData":[OSD([sQuery(id+"F10.wireOp",EDGE,"E173.rect.bottom"),sQuery(id+"F10.wireOp",EDGE,"E173.rect.right")])]});
            var Q1;
            Q1=makeQuery(id+"F11.opExtrude","SWEPT_EDGE",EDGE,{"disambiguationData":[OSD([sQuery(id+"F10.wireOp",EDGE,"E173.rect.top"),sQuery(id+"F10.wireOp",EDGE,"E173.rect.right")])]});
            var Q2;
            Q2=makeQuery(id+"F11.opExtrude","SWEPT_EDGE",EDGE,{"disambiguationData":[OSD([sQuery(id+"F10.wireOp",EDGE,"E173.rect.bottom"),sQuery(id+"F10.wireOp",EDGE,"E173.rect.left")])]});
            var Q3;
            Q3=makeQuery(id+"F11.opExtrude","SWEPT_EDGE",EDGE,{"disambiguationData":[OSD([sQuery(id+"F10.wireOp",EDGE,"E173.rect.top"),sQuery(id+"F10.wireOp",EDGE,"E173.rect.left")])]});
            fillet(context, id + "F14", {"entities" : qUnion([Q0, Q1, Q2, Q3]), "radius" : 50 * mm, "tangentPropagation" : true, "allowEdgeOverflow" : false});
        }
        {
            var Q0;
            Q0=makeQuery(id+"F11.opExtrude","CAP_FACE",FACE,{"disambiguationData":[OSD([sQuery(id+"F10.wireOp",EDGE,"E173.rect.bottom"),sQuery(id+"F10.wireOp",EDGE,"E173.rect.top"),sQuery(id+"F10.wireOp",EDGE,"E173.rect.left"),sQuery(id+"F10.wireOp",EDGE,"E173.rect.right")])],"isStart":false});
            var sketch = newSketch(context, id + "F15", { "sketchPlane" : qUnion([Q0])});
            skLineSegment(sketch, "E176", {"start": v(0, 0) * mm, "end": v(-750, 0) * mm, "construction": true});
            skLineSegment(sketch, "E177", {"start": v(0, 0) * mm, "end": v(0, 500) * mm, "construction": true});
            skLineSegment(sketch, "E178.rect.bottom", {"start": v(-250, 250) * mm, "end": v(250, 250) * mm, "construction": true});
            skLineSegment(sketch, "E178.rect.top", {"start": v(-250, -250) * mm, "end": v(250, -250) * mm, "construction": true});
            skLineSegment(sketch, "E178.rect.left", {"start": v(-250, 250) * mm, "end": v(-250, -250) * mm, "construction": true});
            skLineSegment(sketch, "E178.rect.right", {"start": v(250, 250) * mm, "end": v(250, -250) * mm, "construction": true});
            skPoint(sketch, "E178.rect.middle", {"position": v(0, 0) * mm});
            skLineSegment(sketch, "E179.rect.bottom", {"start": v(-287.5, 212.5) * mm, "end": v(-212.5, 212.5) * mm, "construction": true});
            skLineSegment(sketch, "E179.rect.top", {"start": v(-287.5, 287.5) * mm, "end": v(-212.5, 287.5) * mm, "construction": true});
            skLineSegment(sketch, "E179.rect.left", {"start": v(-287.5, 212.5) * mm, "end": v(-287.5, 287.5) * mm, "construction": true});
            skLineSegment(sketch, "E179.rect.right", {"start": v(-212.5, 212.5) * mm, "end": v(-212.5, 287.5) * mm, "construction": true});
            skPoint(sketch, "E179.rect.middle", {"position": v(-250, 250) * mm});
            skCircle(sketch, "E180", {"center": v(-287.5, 287.5) * mm, "radius": 12.5 * mm});
            skCircle(sketch, "E181", {"center": v(-212.5, 287.5) * mm, "radius": 12.5 * mm});
            skCircle(sketch, "E182", {"center": v(-287.5, 212.5) * mm, "radius": 12.5 * mm});
            skCircle(sketch, "E183", {"center": v(-212.5, 212.5) * mm, "radius": 12.5 * mm});
            skLineSegment(sketch, "E184.MirrorCS", {"start": v(287.5, 287.5) * mm, "end": v(212.5, 287.5) * mm, "construction": true});
            skCircle(sketch, "E185.MirrorC", {"center": v(212.5, 287.5) * mm, "radius": 12.5 * mm});
            skCircle(sketch, "E186.MirrorC", {"center": v(287.5, 287.5) * mm, "radius": 12.5 * mm});
            skPoint(sketch, "E187.MirrorP", {"position": v(250, 250) * mm});
            skLineSegment(sketch, "E188.MirrorCS", {"start": v(287.5, 212.5) * mm, "end": v(287.5, 287.5) * mm, "construction": true});
            skLineSegment(sketch, "E189.MirrorCS", {"start": v(212.5, 212.5) * mm, "end": v(212.5, 287.5) * mm, "construction": true});
            skLineSegment(sketch, "E190.MirrorCS", {"start": v(287.5, 212.5) * mm, "end": v(212.5, 212.5) * mm, "construction": true});
            skCircle(sketch, "E191.MirrorC", {"center": v(212.5, 212.5) * mm, "radius": 12.5 * mm});
            skCircle(sketch, "E192.MirrorC", {"center": v(287.5, 212.5) * mm, "radius": 12.5 * mm});
            skCircle(sketch, "E193.MirrorC", {"center": v(287.5, -287.5) * mm, "radius": 12.5 * mm});
            skCircle(sketch, "E194.MirrorC", {"center": v(212.5, -287.5) * mm, "radius": 12.5 * mm});
            skCircle(sketch, "E195.MirrorC", {"center": v(-212.5, -287.5) * mm, "radius": 12.5 * mm});
            skCircle(sketch, "E196.MirrorC", {"center": v(-287.5, -287.5) * mm, "radius": 12.5 * mm});
            skCircle(sketch, "E197.MirrorC", {"center": v(287.5, -212.5) * mm, "radius": 12.5 * mm});
            skCircle(sketch, "E198.MirrorC", {"center": v(212.5, -212.5) * mm, "radius": 12.5 * mm});
            skCircle(sketch, "E199.MirrorC", {"center": v(-212.5, -212.5) * mm, "radius": 12.5 * mm});
            skCircle(sketch, "E200.MirrorC", {"center": v(-287.5, -212.5) * mm, "radius": 12.5 * mm});
            skLineSegment(sketch, "E201.MirrorCS", {"start": v(287.5, -287.5) * mm, "end": v(212.5, -287.5) * mm, "construction": true});
            skLineSegment(sketch, "E202.MirrorCS", {"start": v(-287.5, -287.5) * mm, "end": v(-212.5, -287.5) * mm, "construction": true});
            skLineSegment(sketch, "E203.MirrorCS", {"start": v(-250, -250) * mm, "end": v(250, -250) * mm});
            skLineSegment(sketch, "E204.MirrorCS", {"start": v(287.5, -212.5) * mm, "end": v(287.5, -287.5) * mm, "construction": true});
            skLineSegment(sketch, "E205.MirrorCS", {"start": v(212.5, -212.5) * mm, "end": v(212.5, -287.5) * mm, "construction": true});
            skLineSegment(sketch, "E206.MirrorCS", {"start": v(-212.5, -212.5) * mm, "end": v(-212.5, -287.5) * mm, "construction": true});
            skLineSegment(sketch, "E207.MirrorCS", {"start": v(-287.5, -212.5) * mm, "end": v(-287.5, -287.5) * mm, "construction": true});
            skPoint(sketch, "E208.MirrorP", {"position": v(250, -250) * mm});
            skPoint(sketch, "E209.MirrorP", {"position": v(-250, -250) * mm});
            skLineSegment(sketch, "E210.MirrorCS", {"start": v(287.5, -212.5) * mm, "end": v(212.5, -212.5) * mm, "construction": true});
            skLineSegment(sketch, "E211.MirrorCS", {"start": v(-287.5, -212.5) * mm, "end": v(-212.5, -212.5) * mm, "construction": true});
            skLineSegment(sketch, "E212", {"start": v(-430, 563.84) * mm, "end": v(-430, -343.41) * mm, "construction": true});
            skLineSegment(sketch, "E213", {"start": v(430, 575.95) * mm, "end": v(430, -602.61) * mm, "construction": true});
            skCircle(sketch, "E214.MirrorC", {"center": v(-647.5, 212.5) * mm, "radius": 12.5 * mm});
            skCircle(sketch, "E215.MirrorC", {"center": v(-572.5, -212.5) * mm, "radius": 12.5 * mm});
            skCircle(sketch, "E216.MirrorC", {"center": v(-572.5, -287.5) * mm, "radius": 12.5 * mm});
            skCircle(sketch, "E217.MirrorC", {"center": v(-572.5, 287.5) * mm, "radius": 12.5 * mm});
            skCircle(sketch, "E218.MirrorC", {"center": v(-647.5, 287.5) * mm, "radius": 12.5 * mm});
            skCircle(sketch, "E219.MirrorC", {"center": v(-572.5, 212.5) * mm, "radius": 12.5 * mm});
            skCircle(sketch, "E220.MirrorC", {"center": v(-647.5, -287.5) * mm, "radius": 12.5 * mm});
            skCircle(sketch, "E221.MirrorC", {"center": v(-647.5, -212.5) * mm, "radius": 12.5 * mm});
            skPoint(sketch, "E222.MirrorP", {"position": v(-610, 250) * mm});
            skLineSegment(sketch, "E223.MirrorCS", {"start": v(-647.5, -212.5) * mm, "end": v(-647.5, -287.5) * mm, "construction": true});
            skLineSegment(sketch, "E224.MirrorCS", {"start": v(-610, 250) * mm, "end": v(-610, -250) * mm, "construction": true});
            skLineSegment(sketch, "E225.MirrorCS", {"start": v(-572.5, 287.5) * mm, "end": v(-647.5, 287.5) * mm, "construction": true});
            skLineSegment(sketch, "E226.MirrorCS", {"start": v(-572.5, 212.5) * mm, "end": v(-572.5, 287.5) * mm, "construction": true});
            skLineSegment(sketch, "E227.MirrorCS", {"start": v(-572.5, -287.5) * mm, "end": v(-647.5, -287.5) * mm, "construction": true});
            skLineSegment(sketch, "E228.MirrorCS", {"start": v(-572.5, -212.5) * mm, "end": v(-647.5, -212.5) * mm, "construction": true});
            skLineSegment(sketch, "E229.MirrorCS", {"start": v(-572.5, -212.5) * mm, "end": v(-572.5, -287.5) * mm, "construction": true});
            skLineSegment(sketch, "E230.MirrorCS", {"start": v(-572.5, 212.5) * mm, "end": v(-647.5, 212.5) * mm, "construction": true});
            skLineSegment(sketch, "E231.MirrorCS", {"start": v(-647.5, 212.5) * mm, "end": v(-647.5, 287.5) * mm, "construction": true});
            skPoint(sketch, "E232.MirrorP", {"position": v(-610, -250) * mm});
            skCircle(sketch, "E233.MirrorC", {"center": v(647.5, 287.5) * mm, "radius": 12.5 * mm});
            skCircle(sketch, "E234.MirrorC", {"center": v(647.5, 212.5) * mm, "radius": 12.5 * mm});
            skCircle(sketch, "E235.MirrorC", {"center": v(572.5, 287.5) * mm, "radius": 12.5 * mm});
            skCircle(sketch, "E236.MirrorC", {"center": v(572.5, -212.5) * mm, "radius": 12.5 * mm});
            skCircle(sketch, "E237.MirrorC", {"center": v(572.5, 212.5) * mm, "radius": 12.5 * mm});
            skCircle(sketch, "E238.MirrorC", {"center": v(647.5, -287.5) * mm, "radius": 12.5 * mm});
            skCircle(sketch, "E239.MirrorC", {"center": v(647.5, -212.5) * mm, "radius": 12.5 * mm});
            skCircle(sketch, "E240.MirrorC", {"center": v(572.5, -287.5) * mm, "radius": 12.5 * mm});
            skLineSegment(sketch, "E241.MirrorCS", {"start": v(610, 250) * mm, "end": v(610, -250) * mm, "construction": true});
            skPoint(sketch, "E242.MirrorP", {"position": v(610, -250) * mm});
            skLineSegment(sketch, "E243.MirrorCS", {"start": v(572.5, 212.5) * mm, "end": v(572.5, 287.5) * mm, "construction": true});
            skLineSegment(sketch, "E244.MirrorCS", {"start": v(572.5, -212.5) * mm, "end": v(647.5, -212.5) * mm, "construction": true});
            skLineSegment(sketch, "E245.MirrorCS", {"start": v(572.5, 212.5) * mm, "end": v(647.5, 212.5) * mm, "construction": true});
            skLineSegment(sketch, "E246.MirrorCS", {"start": v(572.5, -212.5) * mm, "end": v(572.5, -287.5) * mm, "construction": true});
            skPoint(sketch, "E247.MirrorP", {"position": v(610, 250) * mm});
            skLineSegment(sketch, "E248.MirrorCS", {"start": v(572.5, -287.5) * mm, "end": v(647.5, -287.5) * mm, "construction": true});
            skLineSegment(sketch, "E249.MirrorCS", {"start": v(572.5, 287.5) * mm, "end": v(647.5, 287.5) * mm, "construction": true});
            skLineSegment(sketch, "E250.MirrorCS", {"start": v(647.5, 212.5) * mm, "end": v(647.5, 287.5) * mm, "construction": true});
            skLineSegment(sketch, "E251.MirrorCS", {"start": v(647.5, -212.5) * mm, "end": v(647.5, -287.5) * mm, "construction": true});
            skSolve(sketch);
        }
        {
            var Q0;
            Q0=qSketchRegion(id+"F15",true);
            var Q1;
            Q1=makeQuery(id+"F11.opExtrude","CAP_FACE",FACE,{"disambiguationData":[OSD([sQuery(id+"F10.wireOp",EDGE,"E173.rect.bottom"),sQuery(id+"F10.wireOp",EDGE,"E173.rect.top"),sQuery(id+"F10.wireOp",EDGE,"E173.rect.left"),sQuery(id+"F10.wireOp",EDGE,"E173.rect.right")])],"isStart":true});
            extrude(context, id + "F16", {"entities" : qUnion([Q0]), "operationType" : NewBodyOperationType.REMOVE, "endBound" : BoundingType.UP_TO_SURFACE, "oppositeDirection" : true, "endBoundEntityFace" : qUnion([Q1]), "depth" : mm});
        }
        {
            var Q0;
            Q0=makeQuery(id+"F11.opExtrude","CAP_FACE",FACE,{"disambiguationData":[OSD([sQuery(id+"F10.wireOp",EDGE,"E173.rect.bottom"),sQuery(id+"F10.wireOp",EDGE,"E173.rect.top"),sQuery(id+"F10.wireOp",EDGE,"E173.rect.left"),sQuery(id+"F10.wireOp",EDGE,"E173.rect.right")])],"isStart":false});
            var sketch = newSketch(context, id + "F17", { "sketchPlane" : qUnion([Q0])});
            skLineSegment(sketch, "E252", {"start": v(0, 300) * mm, "end": v(0, -500) * mm});
            skPoint(sketch, "E252.startSnap0", {"position": v(0, 500) * mm});
            skLineSegment(sketch, "E253", {"start": v(0, -500) * mm, "end": v(-1, -500) * mm});
            skLineSegment(sketch, "E254", {"start": v(-1, -500) * mm, "end": v(-1, 300) * mm});
            skLineSegment(sketch, "E255", {"start": v(-1, 300) * mm, "end": v(0, 300) * mm});
            skSolve(sketch);
        }
        {
            var Q0;
            Q0 = qSketchRegion(id + "F17", true);
            extrude(context, id + "F18", {"entities" : qUnion([Q0]), "depth" : 1000 * mm});
        }
    });
